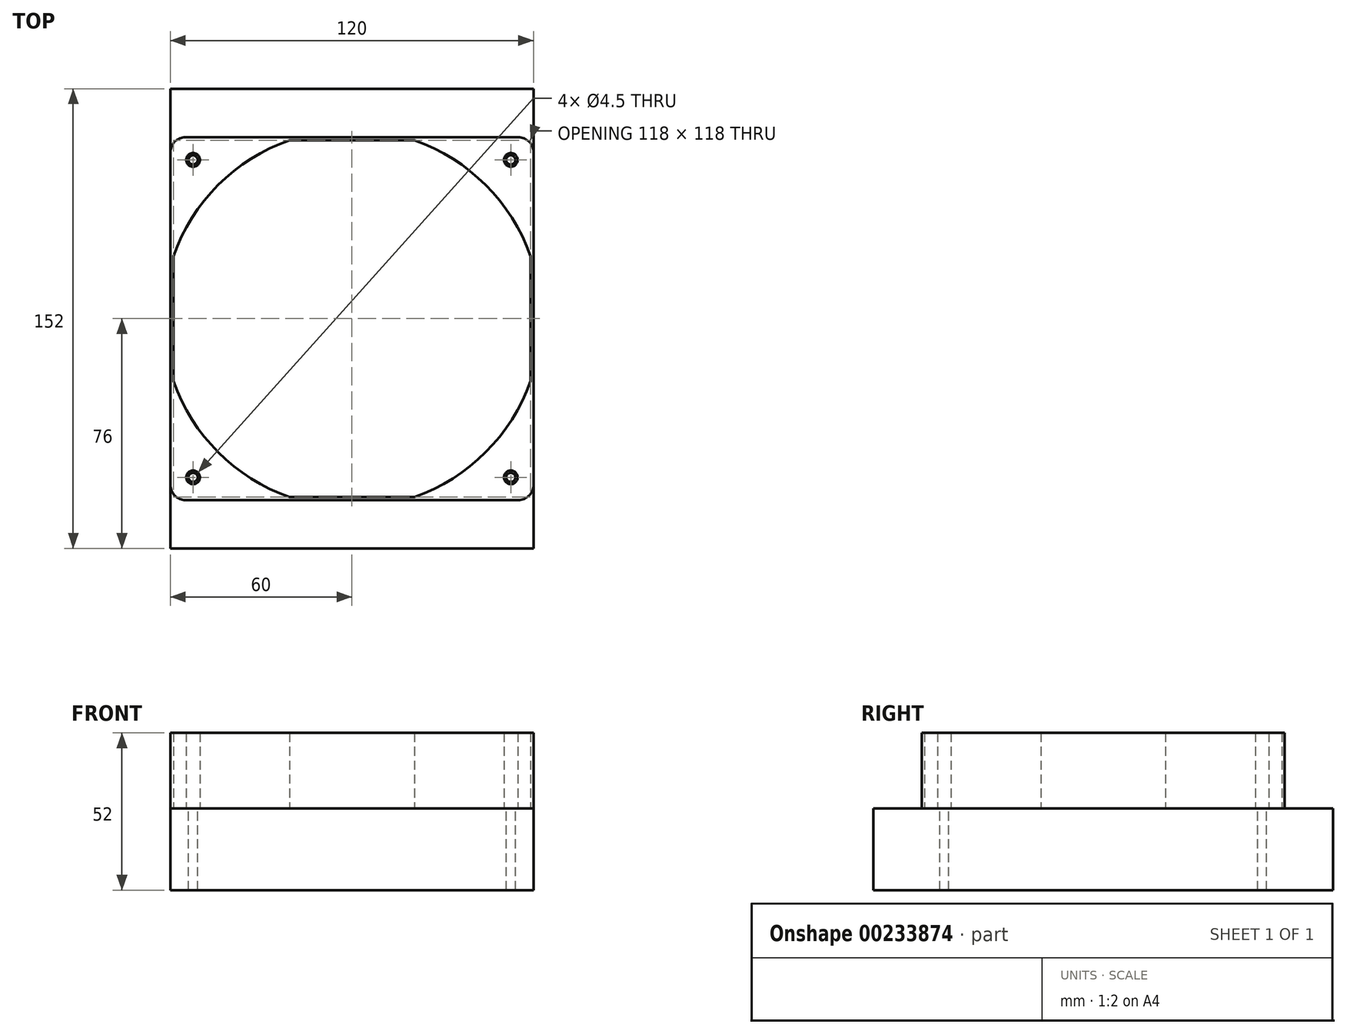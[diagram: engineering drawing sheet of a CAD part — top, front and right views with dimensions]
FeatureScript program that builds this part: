
annotation { "Feature Type Name" : "Feature", "Feature Type Description" : "" }
export const myFeature = defineFeature(function(context is Context, id is Id, definition is map)
    precondition{}
    {
        {
            var Q0;
            Q0=qCreatedBy(makeId("Top.planeOp"),FACE);
            var sketch = newSketch(context, id + "F0", { "sketchPlane" : qUnion([Q0])});
            skLineSegment(sketch, "E0.bottom", {"start": v(55, 60) * mm, "end": v(-55, 60) * mm});
            skLineSegment(sketch, "E0.top", {"start": v(55, -60) * mm, "end": v(-55, -60) * mm});
            skLineSegment(sketch, "E0.left", {"start": v(60, 55) * mm, "end": v(60, -55) * mm});
            skLineSegment(sketch, "E0.right", {"start": v(-60, 55) * mm, "end": v(-60, -55) * mm});
            skPoint(sketch, "E0.middle", {"position": v(0, 0) * mm});
            skCircle(sketch, "E1", {"center": v(-52.5, 52.5) * mm, "radius": 2.25 * mm});
            skCircle(sketch, "E2", {"center": v(52.5, 52.5) * mm, "radius": 2.25 * mm});
            skCircle(sketch, "E3", {"center": v(52.5, -52.5) * mm, "radius": 2.25 * mm});
            skCircle(sketch, "E4", {"center": v(-52.5, -52.5) * mm, "radius": 2.25 * mm});
            skLineSegment(sketch, "E5", {"start": v(-52.5, 52.5) * mm, "end": v(-60, 60) * mm, "construction": true});
            skLineSegment(sketch, "E6", {"start": v(52.5, -52.5) * mm, "end": v(60, -60) * mm, "construction": true});
            skLineSegment(sketch, "E7", {"start": v(52.5, 52.5) * mm, "end": v(60, 60) * mm, "construction": true});
            skArc(sketch, "E8", {"start": v(-20.62, 59) * mm, "mid": v(-44.2, 44.2) * mm, "end": v(-59, 20.62) * mm});
            skLineSegment(sketch, "E9", {"start": v(59, 20.62) * mm, "end": v(59, -20.62) * mm});
            skLineSegment(sketch, "E10", {"start": v(20.62, -59) * mm, "end": v(-20.62, -59) * mm});
            skLineSegment(sketch, "E11", {"start": v(-59, -20.62) * mm, "end": v(-59, 20.62) * mm});
            skLineSegment(sketch, "E12", {"start": v(-20.62, 59) * mm, "end": v(20.62, 59) * mm});
            skArc(sketch, "E13.trimOffspring", {"start": v(59, 20.62) * mm, "mid": v(44.2, 44.2) * mm, "end": v(20.62, 59) * mm});
            skArc(sketch, "E14.trimOffspring", {"start": v(20.62, -59) * mm, "mid": v(44.2, -44.2) * mm, "end": v(59, -20.62) * mm});
            skArc(sketch, "E15.trimOffspring", {"start": v(-59, -20.62) * mm, "mid": v(-44.2, -44.2) * mm, "end": v(-20.62, -59) * mm});
            skPoint(sketch, "E16.visualSharp", {"position": v(-60, 60) * mm});
            skArc(sketch, "E16.filletArc", {"start": v(-55, 60) * mm, "mid": v(-58.54, 58.54) * mm, "end": v(-60, 55) * mm});
            skPoint(sketch, "E17.visualSharp", {"position": v(60, 60) * mm});
            skArc(sketch, "E17.filletArc", {"start": v(60, 55) * mm, "mid": v(58.54, 58.54) * mm, "end": v(55, 60) * mm});
            skPoint(sketch, "E18.visualSharp", {"position": v(60, -60) * mm});
            skArc(sketch, "E18.filletArc", {"start": v(55, -60) * mm, "mid": v(58.54, -58.54) * mm, "end": v(60, -55) * mm});
            skPoint(sketch, "E19.visualSharp", {"position": v(-60, -60) * mm});
            skArc(sketch, "E19.filletArc", {"start": v(-60, -55) * mm, "mid": v(-58.54, -58.54) * mm, "end": v(-55, -60) * mm});
            skSolve(sketch);
        }
        {
            var Q0;
            Q0 = qSketchRegion(id + "F0", true);
            extrude(context, id + "F1", {"entities" : qUnion([Q0]), "depth" : 25 * mm});
        }
        {
            var Q0;
            Q0=qCreatedBy(makeId("Top.planeOp"),FACE);
            var sketch = newSketch(context, id + "F2", { "sketchPlane" : qUnion([Q0])});
            skLineSegment(sketch, "E20.bottom", {"start": v(60, -76) * mm, "end": v(-60, -76) * mm});
            skLineSegment(sketch, "E20.top", {"start": v(60, 76) * mm, "end": v(-60, 76) * mm});
            skLineSegment(sketch, "E20.left", {"start": v(60, -76) * mm, "end": v(60, 76) * mm});
            skLineSegment(sketch, "E20.right", {"start": v(-60, -76) * mm, "end": v(-60, 76) * mm});
            skPoint(sketch, "E20.middle", {"position": v(0, 0) * mm});
            skCircle(sketch, "E21", {"center": v(-52.5, -52.5) * mm, "radius": 1.5 * mm});
            skCircle(sketch, "E22", {"center": v(52.5, -52.5) * mm, "radius": 1.5 * mm});
            skCircle(sketch, "E23", {"center": v(52.5, 52.5) * mm, "radius": 1.5 * mm});
            skCircle(sketch, "E24", {"center": v(-52.5, 52.5) * mm, "radius": 1.5 * mm});
            skSolve(sketch);
        }
        {
            var Q0;
            Q0 = qSketchRegion(id + "F2", true);
            extrude(context, id + "F3", {"entities" : qUnion([Q0]), "oppositeDirection" : true, "depth" : 27 * mm});
        }
    });
